# Revit family: Hager-Orion_Plus-IP65-D300-Cl.II-Poly_double_encl-630A-PL-pl
name_source: partatom
category: Electrical Equipment
units: mm (PartAtom-declared; Revit-internal decimal feet)

## family parameters
Cut with Voids When Loaded = No
Host = Face
Panel Configuration = Two Columns, Circuits Across
Part Type = Panelboard
Room Calculation Point = No
Round Connector Dimension = Use Diameter
Shared = No

## types (6) — shared parameters
EF000003 - Sposób montażu = EV000384 - Montaż natynkowy
EF000007 - Kolor = EV000270 - Szary
EF000049 - Głębokość = 300 mm  [stored 0.984252 ft]
EF000116 - Numer RAL = 7035
EF000266 - Liczba rzędów = 3
EF001131 - Głębokość wewnętrzna = 300 mm  [stored 0.984252 ft]
EF001596 - Materiał obudowy = EV000139 - Tworzywo sztuczne
EF001613 - Podtrzymanie funkcji = EV000494 - Brak
EF004464 - Rodzaj drzwi = EV002646 - Pojedynczy
EF005474 - Stopień ochrony (IP) = EV006421 - IP65
EF006306 - Z zamkiem = Yes
EF007800 - Do ochrony odgromowej = No
EF008873 - Prąd znamionowy (In) = 630 A
EF009170 - Obudowa z materiału o wysokiej wytrzymałości mechanicznej = 2 mm  [stored 0.00656168 ft]
EF009171 - Drzwi/pokrywa z materiału o wysokiej wytrzymałości mechanicznej = 2 mm  [stored 0.00656168 ft]
EF015940 - Pokrywa z wyzwalaczem nadciśnieniowym = No
HG000003 - Zakres = Orion Plus
HG000006 - Montaż podtynkowy = No
HG000010 - Drzwi asymetryczne = No
HG000023 - Obudowa dwusekcyjna = Yes
HG000024 - Wysokość części dolnej = 800 mm  [stored 2.62467 ft]
HG000026 - Stojąca = No
HG000027 - Wysokość cokołu = 70 mm  [stored 0.229659 ft]
Manufacturer = Hager
Type Comments = Orion Plus
zero-valued in all types: Default Elevation, EF000218 - Głębokość wbudowania, EF000437 - Liczba wejść kablowych, EF002950 - Szerokość wyrażona liczbą modułów, EF009554 - Liczba otworów pod flansze

## per-type parameters (varying)
| type | EF000008 - Szerokość | EF000040 - Wysokość | EF000118 - Z płytą montażową | EF000339 - Rodzaj pokrywy | EF001088 - Możliwość rozbudowy | EF003532 - Do zastosowań zewnętrznych | EF004293 - Odporność udarowa | EF004427 - Liczba modułów | EF006244 - Transparentna pokrywa/drzwi | EF009212 - Wykonanie pokrywy | HG000002 - Z drzwiami lub pokrywą | HG000004 - Referencja producenta | HG000009 - Drzwi dwuskrzydłowe |
| Montaż natynkowy IP65 S1100 W1150 G300  - FL360B | 1100 mm | 1150 mm | No | EV004216 - Drzwi | Yes | Yes | EV008784 - IK10 | 138 | Yes | EV009916 - Z otworem | Yes | FL360B | Yes |
| Montaż natynkowy IP65 S1100 W1450 G300  - FL362B | 1100 mm | 1450 mm | No | EV004216 - Drzwi | Yes | Yes | EV008784 - IK10 | 138 | Yes | EV009916 - Z otworem | Yes | FL362B | Yes |
| Montaż natynkowy IP65 S600 W1150 G300  - FL340B | 600 mm | 1150 mm | No | EV004216 - Drzwi | Yes | Yes | EV008784 - IK10 | 69 | Yes | EV009916 - Z otworem | Yes | FL340B | No |
| Montaż natynkowy IP65 S600 W1450 G300  - FL342B | 600 mm | 1450 mm | No | EV004216 - Drzwi | Yes | Yes | EV008784 - IK10 | 69 | Yes | EV009916 - Z otworem | No | FL342B | No |
| Montaż natynkowy IP65 S850 W1150 G300  - FL350B | 850 mm  [stored 2.78871 ft] | 1150 mm | No | EV004216 - Drzwi | Yes | Yes | EV008784 - IK10 | 111 | Yes | EV009916 - Z otworem | Yes | FL350B | No |
| Montaż natynkowy IP65 S850 W1450 G300  - FL352B | 850 mm  [stored 2.78871 ft] | 1450 mm | Yes | EV001012 - Pokrywa | No | No | EV006814 - IK08 | 111 | No | EV000116 - Zamknięty | Yes | FL352B | No |

note: [stored X ft] marks values corroborated as IEEE doubles in the binary element streams (Revit-internal decimal feet)

## geometry (parser evidence)
native form markers: Sweep x10
no freeform markers — native parametric forms only
